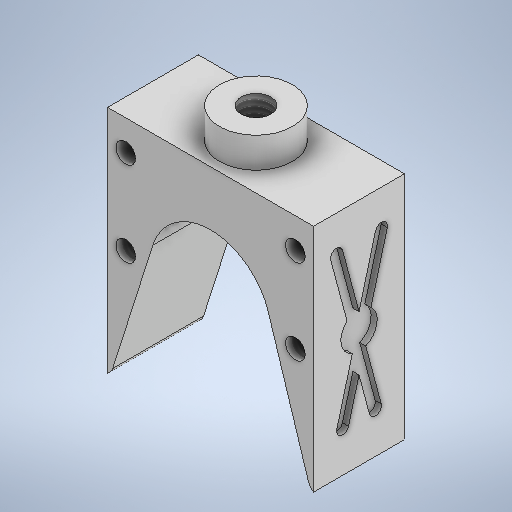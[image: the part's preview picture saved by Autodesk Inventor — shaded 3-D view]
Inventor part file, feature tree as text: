
AUTODESK INVENTOR PART (.ipt)
format: ipt  version: 2025.1 (Build 291241000, 241)  size: 370,688 bytes
history: native  units: mm
features: sketch x7, extrude x4, hole x3, fillet x1, plane x1, mirror x1
ambient origin geometry x8: Origin, YZ Plane, XZ Plane, XY Plane, X Axis, Y Axis, Z Axis, Center Point
bodies: Solid1 (feature_tree)
feature tree (17):
  extrude  "Extrusion1"  Depth=34.0mm
  extrude  "Extrusion2"  Depth=15.0mm
  fillet  "Fillet1"  Radius=16.5mm
  hole  "Hole1"  [1 undecoded]
  hole  "Hole2"  [1 undecoded]
  extrude  "Extrusion3"  Depth=2.0mm
  hole  "Hole3"  [1 undecoded]
  extrude  "Extrusion4"  Depth=1.0mm
  plane  "Work Plane1"
  mirror  "Mirror1"
  sketch  "Sketch1"  dims[d0=34.0mm d1=38.0mm]
  sketch  "Sketch2"  dims[d2=15.0mm d3=0.0mm d4=16.5mm d5=16.5mm]
  sketch  "Sketch3"  dims[d6=10.0mm d7=19.0mm]
  sketch  "Sketch4"  dims[d8=14.0mm d9=0.0mm d10=2.0mm]
  sketch  "Sketch5"  dims[d11=3.242mm d12=14.0mm d13=4.0mm d14=2.0mm d15=90.0deg d16=8.0mm d17=20.594885mm d19=14.0mm]
  sketch  "Sketch6"  dims[d20=14.0mm]
  sketch  "Sketch7"  dims[d21=3.242mm d22=8.0mm d23=4.0mm d24=2.0mm d25=90.0deg d26=8.0mm d27=20.594885mm d28=14.0mm d29=14.0mm d30=5.0mm d31=12.0mm d32=5.0mm d33=0.0mm d34=4.917mm d35=14.0mm d36=4.0mm d37=2.0mm d38=90.0deg d39=15.0mm d40=0.0mm d42=2.0mm d43=2.0mm d44=2.0mm d45=2.0mm d46=12.6mm d47=12.6mm d48=26.0mm d49=26.0mm d50=30.0deg d51=30.0deg d52=3.8mm d53=3.0mm d54=3.0mm d55=13.0mm d56=1.0mm d57=0.0mm d58=-17.0mm d59=19.0mm]
note: 3 required parameter values undecoded (feature->parameter linkage not recoverable at this tier; creation-order binding heuristic only, values carry confidence <= 0.55)
